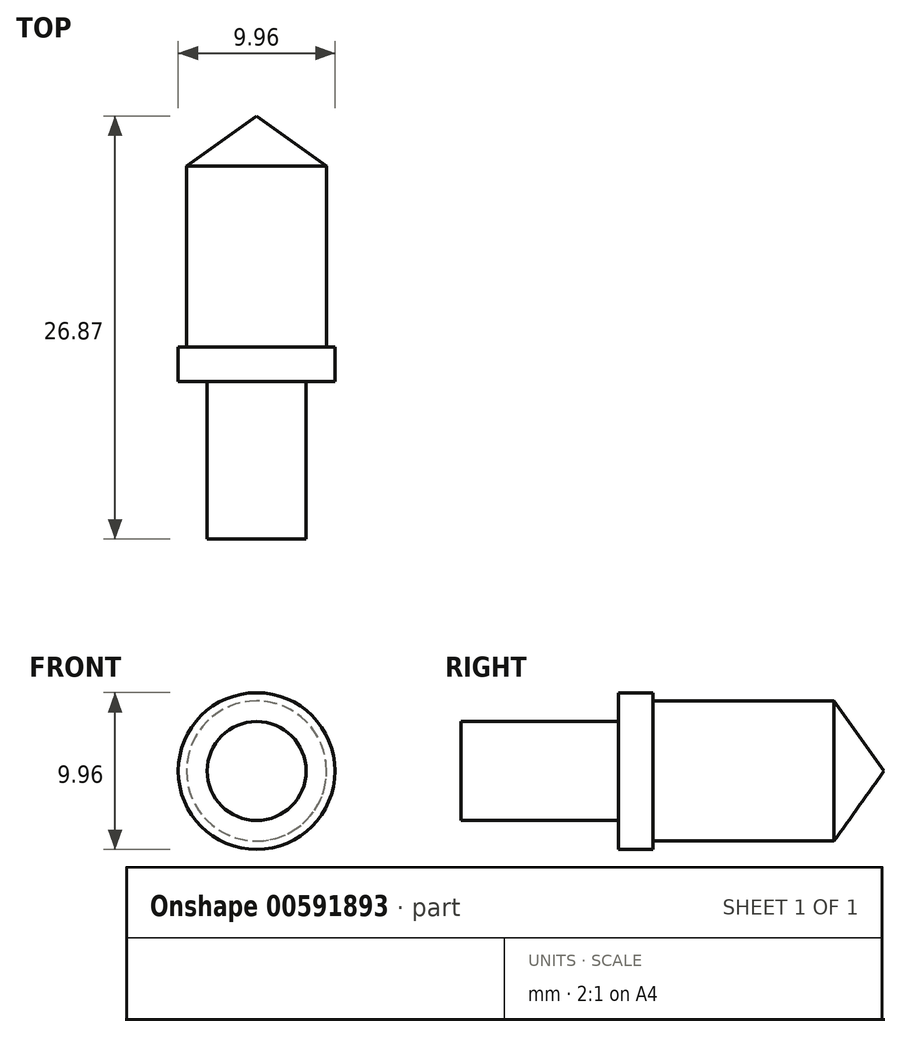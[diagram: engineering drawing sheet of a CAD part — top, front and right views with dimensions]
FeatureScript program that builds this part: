
annotation { "Feature Type Name" : "Feature", "Feature Type Description" : "" }
export const myFeature = defineFeature(function(context is Context, id is Id, definition is map)
    precondition{}
    {
        {
            var Q0;
            Q0=qCreatedBy(makeId("Right.planeOp"),FACE);
            var sketch = newSketch(context, id + "F0", { "sketchPlane" : qUnion([Q0])});
            skLineSegment(sketch, "E0", {"start": v(-26.87, 0) * mm, "end": v(-26.87, 3.14) * mm});
            skLineSegment(sketch, "E1", {"start": v(-26.87, 3.14) * mm, "end": v(-16.87, 3.14) * mm});
            skLineSegment(sketch, "E2", {"start": v(-16.87, 3.14) * mm, "end": v(-16.87, 4.97) * mm});
            skLineSegment(sketch, "E3", {"start": v(-16.87, 4.97) * mm, "end": v(-14.67, 4.97) * mm});
            skLineSegment(sketch, "E4", {"start": v(-14.67, 4.97) * mm, "end": v(-14.67, 4.45) * mm});
            skLineSegment(sketch, "E5", {"start": v(-14.67, 4.45) * mm, "end": v(-3.17, 4.45) * mm});
            skLineSegment(sketch, "E6", {"start": v(-3.17, 4.45) * mm, "end": v(0, 0) * mm});
            skLineSegment(sketch, "E7", {"start": v(0, 0) * mm, "end": v(-26.87, 0) * mm});
            skSolve(sketch);
        }
        {
            var Q0;
            Q0 = qSketchRegion(id + "F0", true);
            var Q1;
            Q1=sQuery(id+"F0.wireOp",EDGE,"E7");
            revolve(context, id + "F1", {"surfaceOperationType" : NewSurfaceOperationType.NEW, "entities" : qUnion([Q0]), "axis" : qUnion([Q1]), "revolveType" : RevolveType.FULL});
        }
    });
